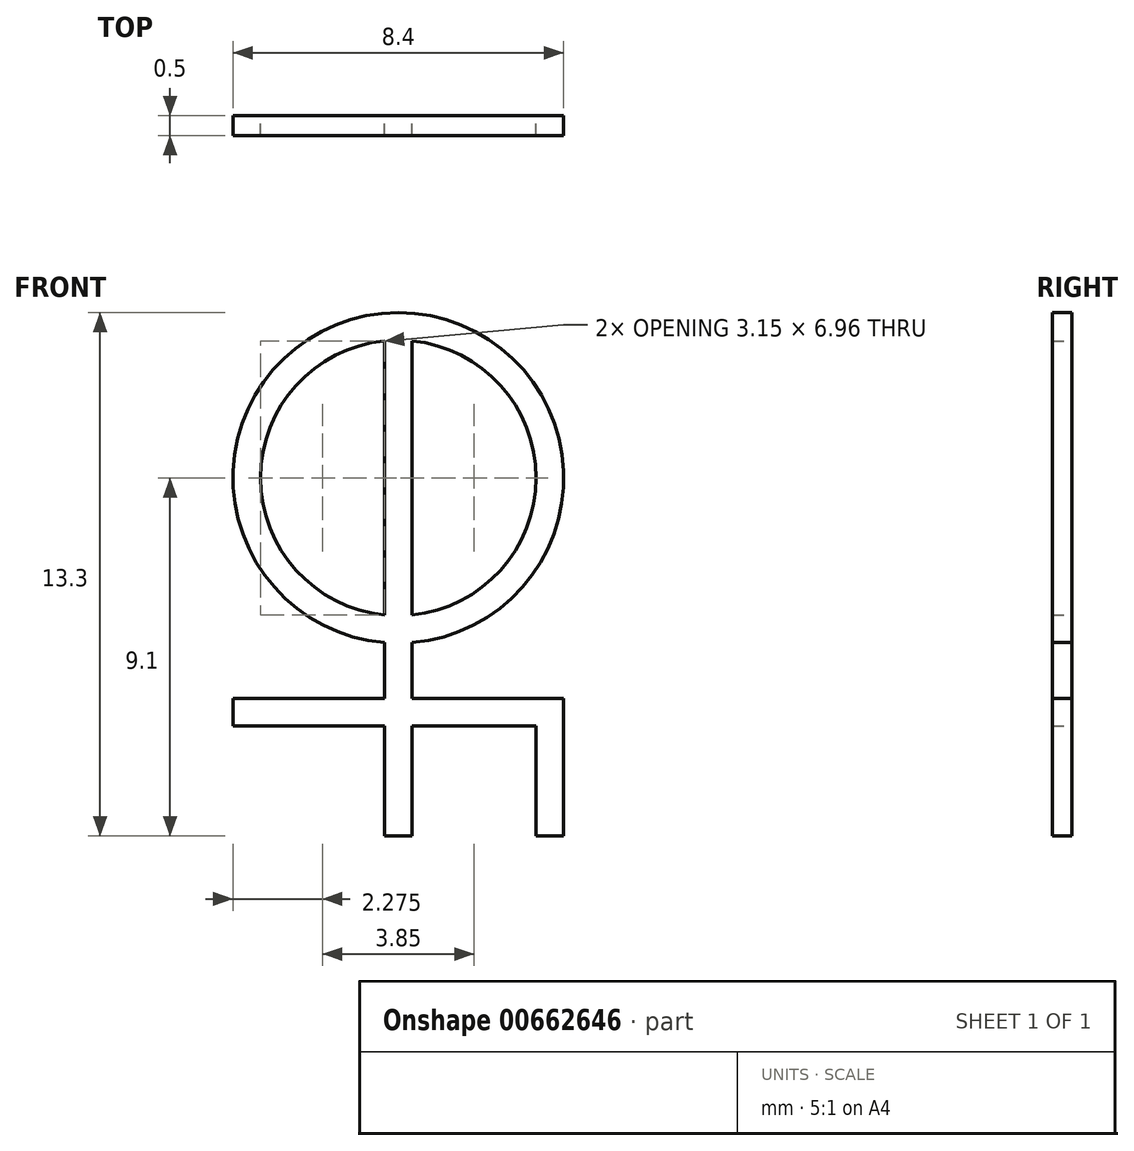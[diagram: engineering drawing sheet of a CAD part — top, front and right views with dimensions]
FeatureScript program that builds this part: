
annotation { "Feature Type Name" : "Feature", "Feature Type Description" : "" }
export const myFeature = defineFeature(function(context is Context, id is Id, definition is map)
    precondition{}
    {
        {
            var Q0;
            Q0=qCreatedBy(makeId("Front.planeOp"),FACE);
            var sketch = newSketch(context, id + "F0", { "sketchPlane" : qUnion([Q0])});
            skArc(sketch, "E0", {"start": v(0.35, -3.48) * mm, "mid": v(3.5, 0) * mm, "end": v(0.35, 3.48) * mm});
            skArc(sketch, "E1.0", {"start": v(0.35, -4.19) * mm, "mid": v(0, 4.2) * mm, "end": v(-0.35, -4.19) * mm});
            skLineSegment(sketch, "E2", {"start": v(-0.35, 3.48) * mm, "end": v(-0.35, -3.48) * mm});
            skLineSegment(sketch, "E3", {"start": v(0.35, 3.48) * mm, "end": v(0.35, -3.48) * mm});
            skLineSegment(sketch, "E4", {"start": v(0.35, -9.1) * mm, "end": v(-0.35, -9.1) * mm});
            skLineSegment(sketch, "E5", {"start": v(-4.2, -5.6) * mm, "end": v(-0.35, -5.6) * mm});
            skLineSegment(sketch, "E6", {"start": v(4.2, -5.6) * mm, "end": v(4.2, -9.1) * mm});
            skLineSegment(sketch, "E7", {"start": v(4.2, -9.1) * mm, "end": v(3.5, -9.1) * mm});
            skLineSegment(sketch, "E8", {"start": v(3.5, -9.1) * mm, "end": v(3.5, -6.3) * mm});
            skLineSegment(sketch, "E9", {"start": v(3.5, -6.3) * mm, "end": v(0.35, -6.3) * mm});
            skLineSegment(sketch, "E10", {"start": v(-4.2, -5.6) * mm, "end": v(-4.2, -6.3) * mm});
            skArc(sketch, "E11.trimOffspring", {"start": v(-0.35, 3.48) * mm, "mid": v(-3.5, 0) * mm, "end": v(-0.35, -3.48) * mm});
            skLineSegment(sketch, "E12.trimOffspring", {"start": v(-0.35, -4.19) * mm, "end": v(-0.35, -5.6) * mm});
            skLineSegment(sketch, "E13.trimOffspring", {"start": v(0.35, -4.19) * mm, "end": v(0.35, -5.6) * mm});
            skLineSegment(sketch, "E14.trimOffspring", {"start": v(-0.35, -6.3) * mm, "end": v(-0.35, -9.1) * mm});
            skLineSegment(sketch, "E15.trimOffspring", {"start": v(0.35, -5.6) * mm, "end": v(4.2, -5.6) * mm});
            skLineSegment(sketch, "E16.trimOffspring", {"start": v(0.35, -6.3) * mm, "end": v(0.35, -9.1) * mm});
            skLineSegment(sketch, "E17.trimOffspring", {"start": v(-0.35, -6.3) * mm, "end": v(-4.2, -6.3) * mm});
            skSolve(sketch);
        }
        {
            var Q0;
            Q0=makeQuery(id+"F0.imprint","IMPRINT",FACE,{"disambiguationData":[TD([[makeQuery(id+"F0.imprint","IMPRINT",EDGE,{"derivedFrom":sQuery(id+"F0.wireOp",EDGE,"E0")}),-1.0]])]});
            extrude(context, id + "F1", {"entities" : qUnion([Q0]), "depth" : .5 * mm, "offsetDistance" : 25 * mm});
        }
    });
